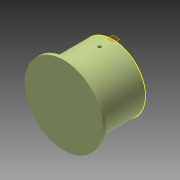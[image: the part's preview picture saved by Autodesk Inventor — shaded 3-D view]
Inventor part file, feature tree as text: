
AUTODESK INVENTOR PART (.ipt)
format: ipt  version: 2013 (Build 170138000, 138)  size: 138,752 bytes
history: native  units: mm
features: sketch x4, hole x2, revolve x1, plane x1
ambient origin geometry x8: Origin, YZ Plane, XZ Plane, XY Plane, X Axis, Y Axis, Z Axis, Center Point
bodies: Volumenkörper1 (feature_tree)
feature tree (8):
  revolve  "Umdrehung1"
  hole  "Bohrung1"  [1 undecoded]
  sketch  "Skizze3"  dims[d5=10.0mm]
  plane  "Arbeitsebene1"
  hole  "Bohrung2"  [1 undecoded]
  sketch  "Skizze1"  dims[d0=120.0mm d2=100.0mm]
  sketch  "Skizze2"  dims[d3=30.0mm d4=50.0mm]
  sketch  "Skizze4"  dims[d6=150.0mm d7=90.0deg d8=140.0mm d10=120.0mm d11=10.0mm d12=3.5mm d13=10.0mm d14=3.5mm d16=3.5mm d17=3.5mm d18=3.5mm d19=3.5mm d20=3.5mm d21=3.5mm d22=10.0mm d23=10.0mm d24=10.0mm d25=10.0mm d26=10.0mm d27=10.0mm d28=3.242mm d29=8.0mm d30=4.0mm d31=2.0mm d32=90.0deg d33=12.0mm d34=20.594885mm d35=40.0mm d36=100.0mm d37=10.0mm d38=8.0mm d39=4.0mm d40=2.0mm d41=90.0deg d42=100.0mm d43=20.594885mm]
note: 2 required parameter values undecoded (feature->parameter linkage not recoverable at this tier; creation-order binding heuristic only, values carry confidence <= 0.55)
